# Revit family: Graypants_Roest_75h_150h_Pendant_R21_0925
name_source: partatom
category: Lighting Fixtures
units: mm (PartAtom-declared; Revit-internal decimal feet)

## family parameters
Cut with Voids When Loaded = No
Host = Face
Light Source = Yes
Part Type = Normal
Room Calculation Point = No
Round Connector Dimension = Use Diameter
Shared = No

## types (2) — shared parameters
Color Filter = 16777215
Default Elevation = 4' - 0"
Dimming Lamp Color Temperature Shift = <None>
Graypants_Apparent_Load = GU10, Max 10W LED | 
Optional Integrated LED - 12W
Graypants_Cable_Material_Finish = _Graypants_Steel
Graypants_Canopy_Material_Finish = _Graypants_Black_Finish
Graypants_Cord/Canopy_Finish_Options = Black
Graypants_Cord_Material_Finish = _Graypants_Black_Finish
Graypants_Description = The Roest collection bends the norm with its unpretentious simplicity, in which the design has met no equal. Nature’s reaction between 
iron, oxygen, water and time. Designed by VanJoost and hand-made in Holland, Roest presents natural colors in unusual settings.
Graypants_Dimming = GU10 - Depending on lamp | 
Optional Integrated LED - 0-10v or Triac/ELV
Graypants_Initial_Intensity = GU10 - Dependant on Lamp | 
Optional Integrated LED - NA
Graypants_Manufacturer = Graypants
Graypants_Shade_Finish_Options = Rust
 | Zinc
 | Carbon
Graypants_Spec_Sheet = https://www.dropbox.com
Graypants_URL = www.graypants.com
Graypants_Voltage = GU10 - 120V | Optional Integrated LED - 120-277V
Light Source Symbol Size = 1' - 7"

## per-type parameters (varying)
| type | Emit from Line Length | Graypants_150h_Cable_Visible | Graypants_150h_Canopy_Visible | Graypants_150h_Cords_Visible | Graypants_150h_Shade_Visible | Graypants_75h_Cable_Visible | Graypants_75h_Canopy_Visible | Graypants_75h_Cords_Visible | Graypants_75h_Shade_Visible | Graypants_Initial_Color_Temperature | Graypants_Model | Graypants_SKU |
| Graypants_Roest_75h_Pendant | 2' - 5 7/32" | No | No | No | No | Yes | Yes | Yes | Yes | GU10 - 2700K Recommended / Dependant on Lamp / Integrated LED - 2700K | 75h Pendant | 75h Pendant Zinc - GP2003-AZ
 / 75h Pendant Carbon - GP2003-C / 75h Pendant Carbon - GP2003-C
 / 75h Pendant Rust - GP2003 -N |
| Graypants_Roest_150h_Pendant | 2' - 0" | Yes | Yes | Yes | Yes | No | No | No | No | GU10 - 2700K Recommended / Dependant on Lamp / 
Integrated LED - 2700K | 150h Pendant | 150h Pendant Zinc - GP2004-AZ
 / 150h Pendant Carbon - GP2004-C
 / 150h Pendant Rust - GP2004-N |

## geometry (parser evidence)
native form markers: Sweep x10
no freeform markers — native parametric forms only
